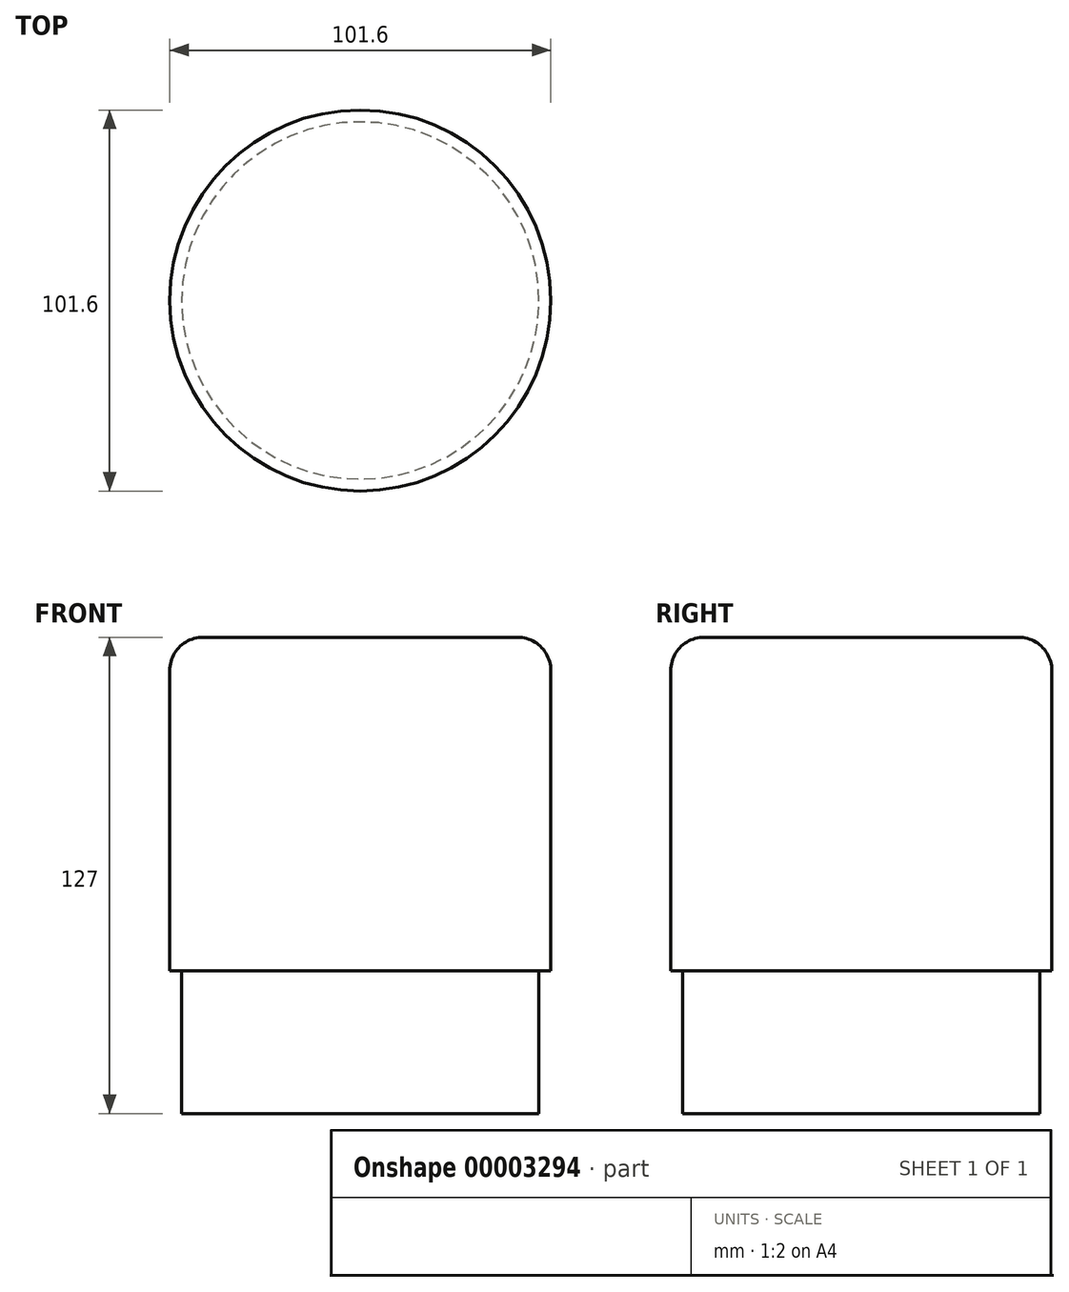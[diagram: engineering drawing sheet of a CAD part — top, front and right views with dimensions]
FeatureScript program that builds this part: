
annotation { "Feature Type Name" : "Feature", "Feature Type Description" : "" }
export const myFeature = defineFeature(function(context is Context, id is Id, definition is map)
    precondition{}
    {
        {
            var Q0;
            Q0=qCreatedBy(makeId("Top.planeOp"),FACE);
            var sketch = newSketch(context, id + "F0", { "sketchPlane" : qUnion([Q0])});
            skCircle(sketch, "E0", {"center": v(0, 0) * mm, "radius": 50.8 * mm});
            skSolve(sketch);
        }
        {
            var Q0;
            Q0=makeQuery(id+"F0.imprint","IMPRINT",FACE,{"disambiguationData":[TD([[makeQuery(id+"F0.imprint","IMPRINT",EDGE,{"derivedFrom":sQuery(id+"F0.wireOp",EDGE,"E0")}),1.0]])]});
            extrude(context, id + "F1", {"entities" : qUnion([Q0]), "depth" : 88.9 * mm});
        }
        {
            var Q0;
            Q0=makeQuery(id+"F1.opExtrude","CAP_EDGE",EDGE,{"disambiguationData":[OSD([sQuery(id+"F0.wireOp",EDGE,"E0")])],"isStart":false});
            fillet(context, id + "F2", {"entities" : qUnion([Q0]), "radius" : 8.9 * mm, "tangentPropagation" : true, "allowEdgeOverflow" : false});
        }
        {
            var Q0;
            Q0=makeQuery(id+"F1.opExtrude","CAP_FACE",FACE,{"disambiguationData":[OSD([sQuery(id+"F0.wireOp",EDGE,"E0")])],"isStart":true});
            var sketch = newSketch(context, id + "F3", { "sketchPlane" : qUnion([Q0])});
            skCircle(sketch, "E1", {"center": v(0, 0) * mm, "radius": 47.62 * mm});
            skSolve(sketch);
        }
        {
            var Q0;
            Q0=makeQuery(id+"F3.imprint","IMPRINT",FACE,{"disambiguationData":[TD([[makeQuery(id+"F3.imprint","IMPRINT",EDGE,{"derivedFrom":sQuery(id+"F3.wireOp",EDGE,"E1")}),1.0]])]});
            extrude(context, id + "F4", {"entities" : qUnion([Q0]), "operationType" : NewBodyOperationType.ADD, "depth" : 38.1 * mm});
        }
    });
